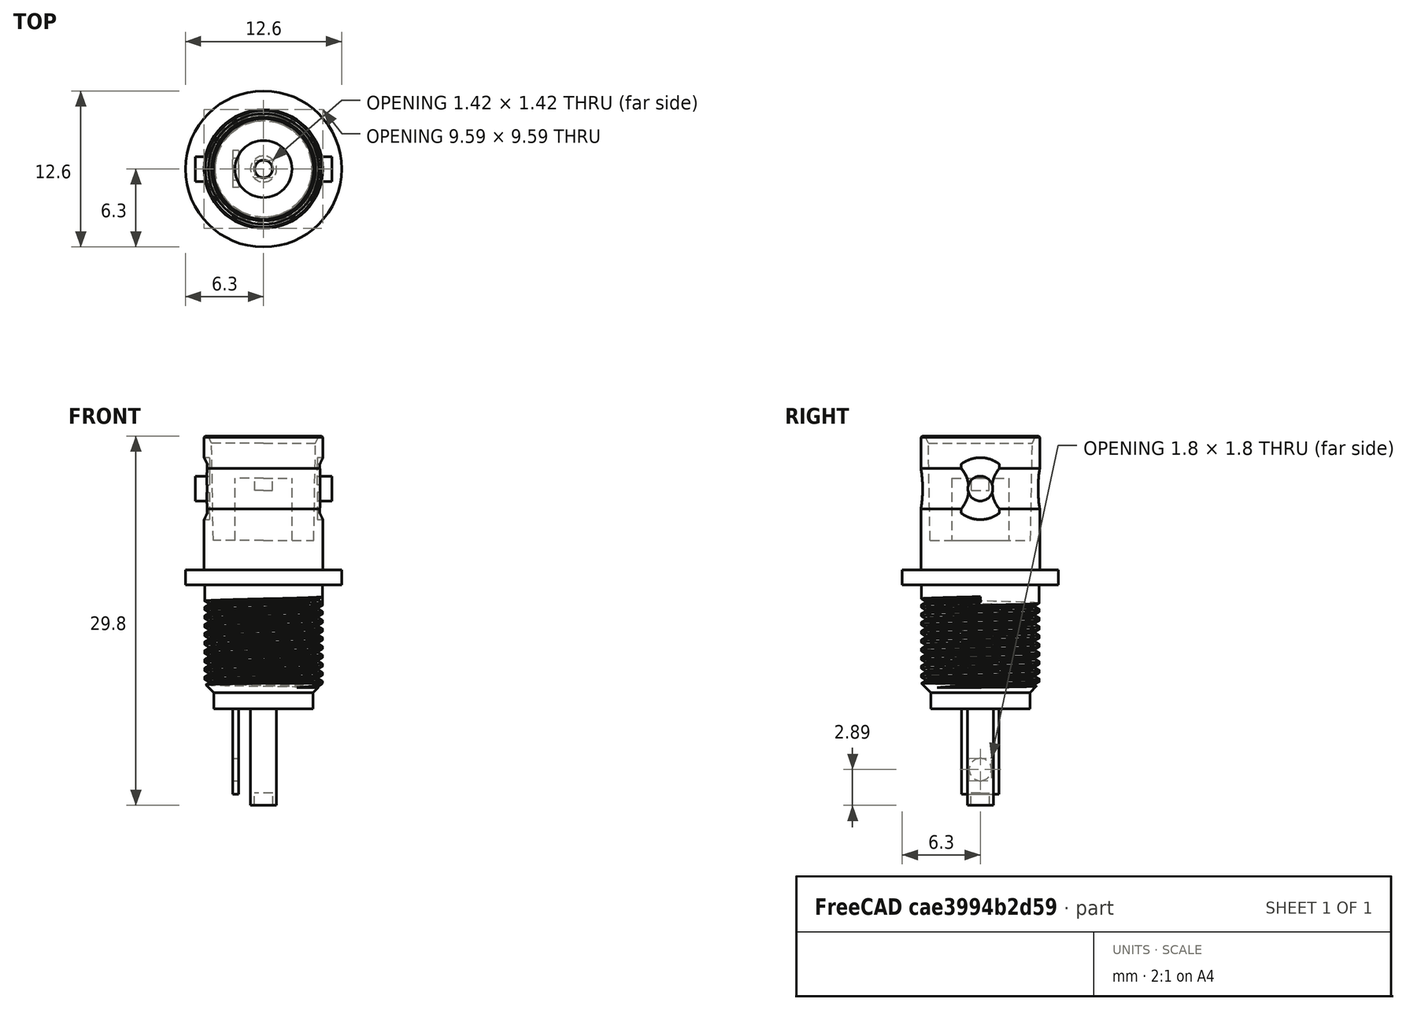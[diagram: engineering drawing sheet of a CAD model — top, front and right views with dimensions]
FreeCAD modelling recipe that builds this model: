
FCSTD DOCUMENT  (FreeCAD 0.19R24267 +148 (Git))
Label: bnc_002
License: Public Domain
LicenseURL: http://en.wikipedia.org/wiki/Public_domain
objects: Part::Feature×1, Spreadsheet::Sheet×1, Sketcher::SketchObject×1, PartDesign::Body×1, App::Part×1
note: 3 computed .brp shape members not serialized (recipe doc carries the construction recipe); baked Part::Feature solids carry a one-line shape summary decoded from their .brp

FEATURE [Part::Feature] Solid  label="BNCEmbaseStep"
  Placement = pos=(0,0,12) rot=(0,0,1;0rad)
  shape: bbox 16.02 x 16.37 x 32.65 mm, 116 faces (baked)
FEATURE [Spreadsheet::Sheet] Spreadsheet  label="bnc"
  cells = A2=trouDiam; B2(trouDiam)=9.699999999999999; A3=trouMeplat; B3(trouMeplat)=8.699999999999999; A4=trouJeu; B4(trouJeu)=0.6; A5=trouMeplatDepuisLeCentre; B5(trouMeplatDepuisLeCentre)=3.35
FEATURE [Sketcher::SketchObject] Sketch  label="sk_trou"
  FullyConstrained = true
  MapMode = 5
  Support = -> [XY_Plane001]
  expr: Constraints[1] = <<bnc>>.trouDiam + <<bnc>>.trouJeu
  expr: Constraints[5] = <<bnc>>.trouMeplatDepuisLeCentre + <<bnc>>.trouJeu
  sketch-geometry (2):
    g0: ArcOfCircle CenterX=0 CenterY=0 CenterZ=0 NormalX=0 NormalY=0 NormalZ=1 AngleXU=0 Radius=5.15 StartAngle=0.696659 EndAngle=5.58653
    g1: LineSegment StartX=3.95 StartY=3.30454 StartZ=0 EndX=3.95 EndY=-3.30454 EndZ=0
  constraints (6):
    c: Coincident(g0,g-1)
    c: Diameter(g0) = 10.3
    c: Vertical(g1)
    c: Coincident(g0,g1)
    c: Coincident(g0,g1)
    c: DistanceX(g0,g0) = 3.95
FEATURE [PartDesign::Body] Body  label="bncBodyPourTrou"
  Group = -> [Sketch]
  Origin = -> Origin001
FEATURE [App::Part] Part  label="BNC_embase"
  Group = -> [Spreadsheet,Solid,Body]
  Origin = -> Origin
